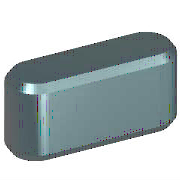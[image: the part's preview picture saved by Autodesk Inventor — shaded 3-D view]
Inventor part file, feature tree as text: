
AUTODESK INVENTOR PART (.ipt)
format: ipt  version: 2025 (Build 290162000, 162)  size: 136,704 bytes
history: native  units: mm (DEFAULTED — no unit token found)
features: plane x3, extrude x1
ambient origin geometry x8: Origin, YZ Plane, XZ Plane, XY Plane, X Axis, Y Axis, Z Axis, Center Point
bodies: Solid1 (feature_tree)
feature tree (4):
  plane  "Work Plane1"
  plane  "Work Plane2"
  extrude  "轴承体1"  Depth=7.0mm
  plane  "Work Plane3"
